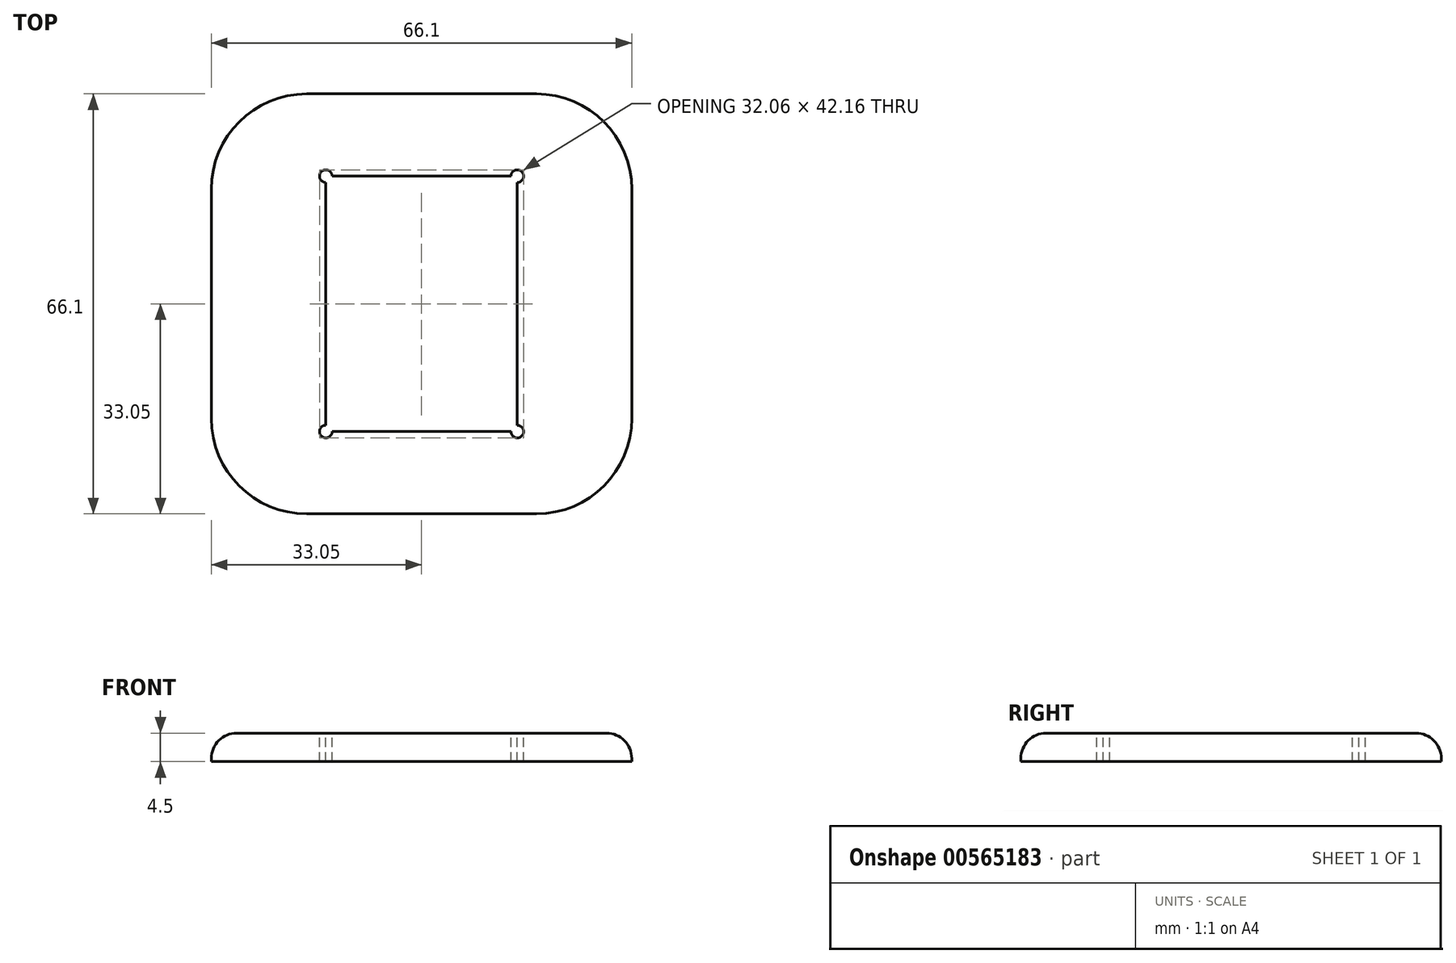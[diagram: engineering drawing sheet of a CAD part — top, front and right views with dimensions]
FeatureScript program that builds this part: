
annotation { "Feature Type Name" : "Feature", "Feature Type Description" : "" }
export const myFeature = defineFeature(function(context is Context, id is Id, definition is map)
    precondition{}
    {
        {
            var Q0;
            Q0=qCreatedBy(makeId("Top.planeOp"),FACE);
            var sketch = newSketch(context, id + "F0", { "sketchPlane" : qUnion([Q0])});
            skLineSegment(sketch, "E0.bottom", {"start": v(15.05, 20.1) * mm, "end": v(-15.05, 20.1) * mm});
            skLineSegment(sketch, "E0.top", {"start": v(15.05, -20.1) * mm, "end": v(-15.05, -20.1) * mm});
            skLineSegment(sketch, "E0.left", {"start": v(15.05, 20.1) * mm, "end": v(15.05, -20.1) * mm});
            skLineSegment(sketch, "E0.right", {"start": v(-15.05, 20.1) * mm, "end": v(-15.05, -20.1) * mm});
            skPoint(sketch, "E0.middle", {"position": v(0, 0) * mm});
            skLineSegment(sketch, "E1.bottom", {"start": v(33.05, 33.05) * mm, "end": v(-33.05, 33.05) * mm});
            skLineSegment(sketch, "E1.top", {"start": v(33.05, -33.05) * mm, "end": v(-33.05, -33.05) * mm});
            skLineSegment(sketch, "E1.left", {"start": v(33.05, 33.05) * mm, "end": v(33.05, -33.05) * mm});
            skLineSegment(sketch, "E1.right", {"start": v(-33.05, 33.05) * mm, "end": v(-33.05, -33.05) * mm});
            skSolve(sketch);
        }
        {
            var Q0;
            Q0=makeQuery(id+"F0.imprint","IMPRINT",FACE,{"disambiguationData":[TD([[makeQuery(id+"F0.imprint","IMPRINT",EDGE,{"derivedFrom":sQuery(id+"F0.wireOp",EDGE,"E0.bottom")}),-1.0]])]});
            extrude(context, id + "F1", {"entities" : qUnion([Q0]), "depth" : 4.5 * mm, "offsetDistance" : 25 * mm});
        }
        {
            var Q0;
            Q0=makeQuery(id+"F1.opExtrude","SWEPT_EDGE",EDGE,{"disambiguationData":[OSD([sQuery(id+"F0.wireOp",EDGE,"E1.top"),sQuery(id+"F0.wireOp",EDGE,"E1.right")])]});
            var Q1;
            Q1=makeQuery(id+"F1.opExtrude","SWEPT_EDGE",EDGE,{"disambiguationData":[OSD([sQuery(id+"F0.wireOp",EDGE,"E1.top"),sQuery(id+"F0.wireOp",EDGE,"E1.left")])]});
            var Q2;
            Q2=makeQuery(id+"F1.opExtrude","SWEPT_EDGE",EDGE,{"disambiguationData":[OSD([sQuery(id+"F0.wireOp",EDGE,"E1.bottom"),sQuery(id+"F0.wireOp",EDGE,"E1.right")])]});
            var Q3;
            Q3=makeQuery(id+"F1.opExtrude","SWEPT_EDGE",EDGE,{"disambiguationData":[OSD([sQuery(id+"F0.wireOp",EDGE,"E1.bottom"),sQuery(id+"F0.wireOp",EDGE,"E1.left")])]});
            fillet(context, id + "F2", {"entities" : qUnion([Q0, Q1, Q2, Q3]), "radius" : 15 * mm, "tangentPropagation" : true, "allowEdgeOverflow" : false});
        }
        {
            var Q0;
            {var subQ0=sQuery(id+"F0.wireOp",EDGE,"E1.right");var subQ1=sQuery(id+"F0.wireOp",EDGE,"E1.bottom");Q0=makeQuery(id+"F2.opFillet","BLEND_EDGE",EDGE,{"blendedFrom":[makeQuery(id+"F1.opExtrude","SWEPT_EDGE",EDGE,{"disambiguationData":[OSD([subQ1,subQ0])]}),makeQuery(id+"F1.opExtrude","CAP_FACE",FACE,{"disambiguationData":[OSD([sQuery(id+"F0.wireOp",EDGE,"E0.bottom"),sQuery(id+"F0.wireOp",EDGE,"E0.top"),sQuery(id+"F0.wireOp",EDGE,"E0.left"),sQuery(id+"F0.wireOp",EDGE,"E0.right"),subQ1,sQuery(id+"F0.wireOp",EDGE,"E1.top"),sQuery(id+"F0.wireOp",EDGE,"E1.left"),subQ0])],"isStart":false})],"blendedInto":[makeQuery(id+"F1.opExtrude","CAP_FACE",FACE,{"disambiguationData":[OSD([sQuery(id+"F0.wireOp",EDGE,"E0.bottom"),sQuery(id+"F0.wireOp",EDGE,"E0.top"),sQuery(id+"F0.wireOp",EDGE,"E0.left"),sQuery(id+"F0.wireOp",EDGE,"E0.right"),subQ1,sQuery(id+"F0.wireOp",EDGE,"E1.top"),sQuery(id+"F0.wireOp",EDGE,"E1.left"),subQ0])],"isStart":false})]});}
            fillet(context, id + "F3", {"entities" : qUnion([Q0]), "radius" : 4 * mm, "tangentPropagation" : true, "allowEdgeOverflow" : false});
        }
        {
            var Q0;
            Q0=makeQuery(id+"F1.opExtrude","CAP_FACE",FACE,{"disambiguationData":[OSD([sQuery(id+"F0.wireOp",EDGE,"E0.bottom"),sQuery(id+"F0.wireOp",EDGE,"E0.top"),sQuery(id+"F0.wireOp",EDGE,"E0.left"),sQuery(id+"F0.wireOp",EDGE,"E0.right"),sQuery(id+"F0.wireOp",EDGE,"E1.bottom"),sQuery(id+"F0.wireOp",EDGE,"E1.top"),sQuery(id+"F0.wireOp",EDGE,"E1.left"),sQuery(id+"F0.wireOp",EDGE,"E1.right")])],"isStart":false});
            var sketch = newSketch(context, id + "F4", { "sketchPlane" : qUnion([Q0])});
            skCircle(sketch, "E2", {"center": v(15.05, 20.1) * mm, "radius": 1 * mm});
            skCircle(sketch, "E3", {"center": v(15.05, -20.1) * mm, "radius": 1 * mm});
            skCircle(sketch, "E4", {"center": v(-15.05, -20.1) * mm, "radius": 1 * mm});
            skCircle(sketch, "E5", {"center": v(-15.05, 20.1) * mm, "radius": 1 * mm});
            skSolve(sketch);
        }
        {
            var Q0;
            Q0 = qSketchRegion(id + "F4", true);
            extrude(context, id + "F5", {"entities" : qUnion([Q0]), "operationType" : NewBodyOperationType.REMOVE, "oppositeDirection" : true, "depth" : 25 * mm, "offsetDistance" : 25 * mm});
        }
    });
